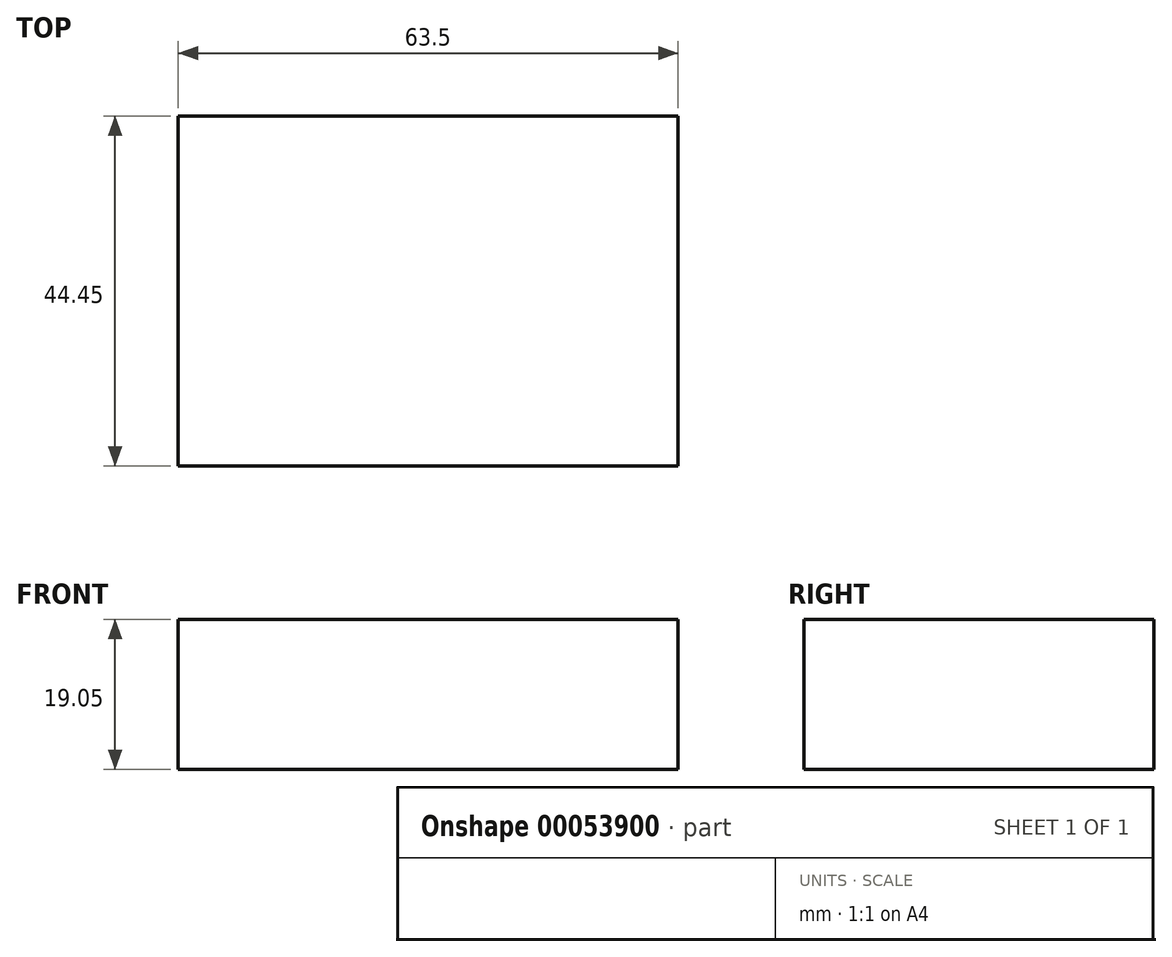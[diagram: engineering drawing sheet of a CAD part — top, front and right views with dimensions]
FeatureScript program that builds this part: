
annotation { "Feature Type Name" : "Feature", "Feature Type Description" : "" }
export const myFeature = defineFeature(function(context is Context, id is Id, definition is map)
    precondition{}
    {
        {
            var Q0;
            Q0=qCreatedBy(makeId("Front.planeOp"),FACE);
            var sketch = newSketch(context, id + "F0", { "sketchPlane" : qUnion([Q0])});
            skLineSegment(sketch, "E0.bottom", {"start": v(-6.45, -31.14) * mm, "end": v(57.05, -31.14) * mm});
            skLineSegment(sketch, "E0.top", {"start": v(-6.45, -50.2) * mm, "end": v(57.05, -50.2) * mm});
            skLineSegment(sketch, "E0.left", {"start": v(-6.45, -31.14) * mm, "end": v(-6.45, -50.2) * mm});
            skLineSegment(sketch, "E0.right", {"start": v(57.05, -31.14) * mm, "end": v(57.05, -50.2) * mm});
            skSolve(sketch);
        }
        {
            var Q0;
            Q0 = qSketchRegion(id + "F0", true);
            extrude(context, id + "F1", {"entities" : qUnion([Q0]), "depth" : 44.45 * mm});
        }
    });
